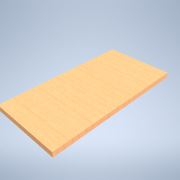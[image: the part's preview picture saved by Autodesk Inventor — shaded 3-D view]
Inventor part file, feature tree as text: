
AUTODESK INVENTOR PART (.ipt)
format: ipt  version: 2021 (Build 250183000, 183)  size: 107,008 bytes
history: native  units: mm
features: extrude x1, sketch x1
ambient origin geometry x8: Origin, YZ Plane, XZ Plane, XY Plane, X Axis, Y Axis, Z Axis, Center Point
bodies: Solid1 (feature_tree)
feature tree (2):
  extrude  "Extrusion1"  [1 undecoded]
  sketch  "Sketch1"  dims[d3=0.0mm]
note: 1 required parameter value undecoded (feature->parameter linkage not recoverable at this tier; creation-order binding heuristic only, values carry confidence <= 0.55)
